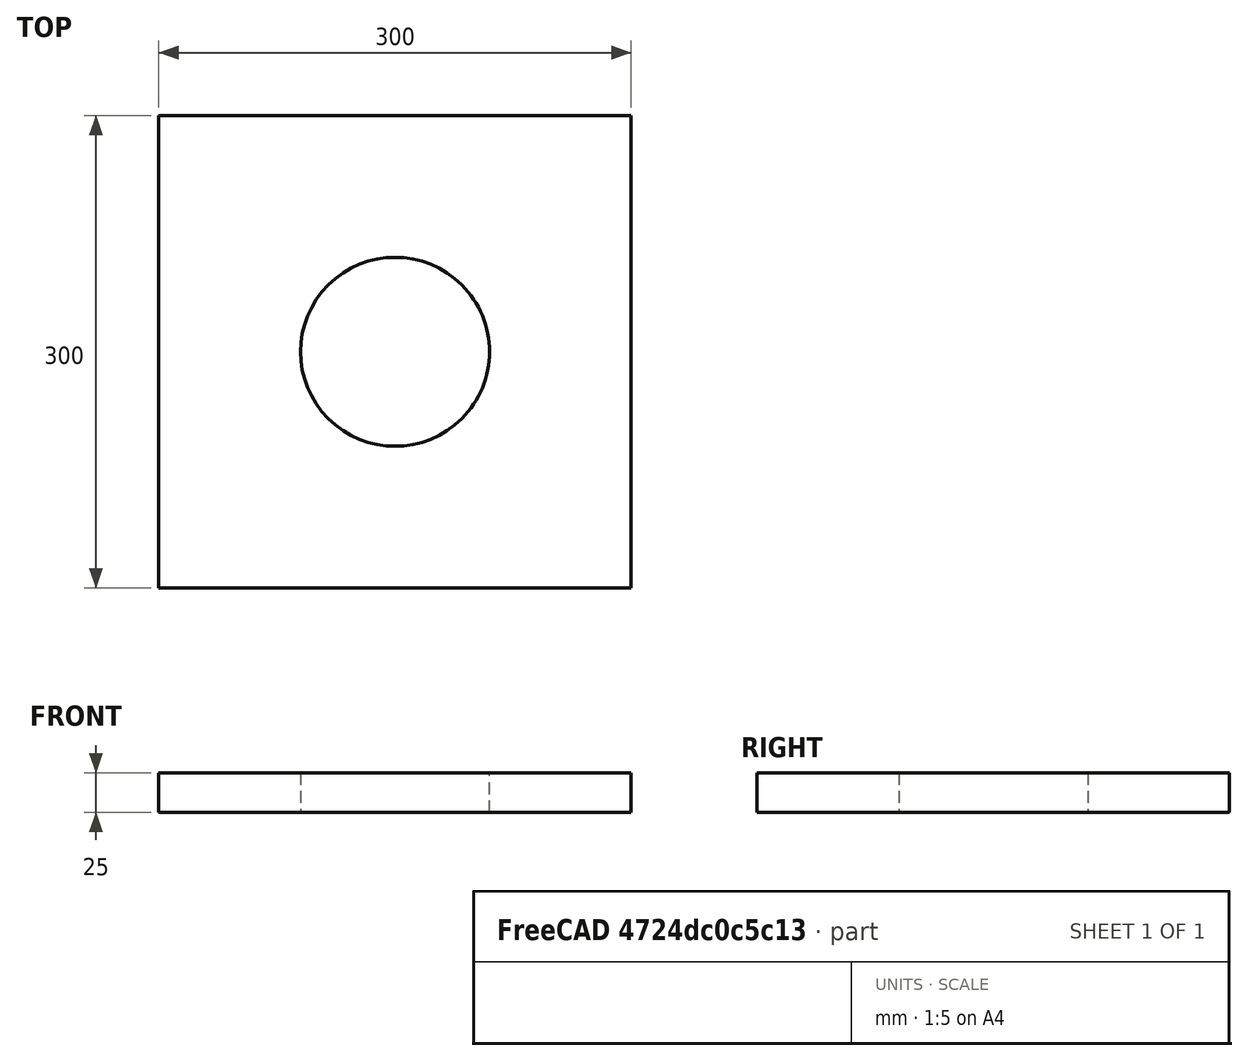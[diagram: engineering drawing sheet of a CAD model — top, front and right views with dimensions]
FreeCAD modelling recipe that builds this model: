
FCSTD DOCUMENT  (FreeCAD 0.21R33694 (Git))
Label: Lug_Displacement_Example
License: All rights reserved
LicenseURL: http://en.wikipedia.org/wiki/All_rights_reserved
objects: Part::FeaturePython×5, Sketcher::SketchObject×2, Part::Extrusion×2, Fem::FemMeshObjectPython×2, Fem::FemSolverObjectPython×1, Fem::ConstraintFixed×1, Fem::ConstraintPressure×1, Part::MultiFuse×1, App::MaterialObjectPython×1, Fem::ConstraintDisplacement×1, Fem::FemResultObjectPython×1, Fem::FemAnalysis×1
note: 10 computed .brp shape members not serialized (recipe doc carries the construction recipe); baked Part::Feature solids carry a one-line shape summary decoded from their .brp

FEATURE [Sketcher::SketchObject] Sketch
  FullyConstrained = true
  Placement = pos=(150,0,0) rot=(0,0,1;0rad)
  sketch-geometry (5):
    g0: LineSegment StartX=0 StartY=0 StartZ=0 EndX=300 EndY=0 EndZ=0
    g1: LineSegment StartX=300 StartY=0 StartZ=0 EndX=300 EndY=300 EndZ=0
    g2: LineSegment StartX=300 StartY=300 StartZ=0 EndX=0 EndY=300 EndZ=0
    g3: LineSegment StartX=0 StartY=300 StartZ=0 EndX=0 EndY=0 EndZ=0
    g4: Circle CenterX=150 CenterY=150 CenterZ=0 NormalX=0 NormalY=0 NormalZ=1 AngleXU=0 Radius=60
  constraints (14):
    c: Coincident(g0,g1)
    c: Coincident(g1,g2)
    c: Coincident(g2,g3)
    c: Coincident(g3,g0)
    c: Horizontal(g0)
    c: Horizontal(g2)
    c: Vertical(g1)
    c: Vertical(g3)
    c: Coincident(g0,g-1)
    c: DistanceY(g1,g1) = 300
    c: DistanceX(g0,g0) = 300
    c: DistanceX(g0,g4) = 150
    c: DistanceY(g0,g4) = 150
    c: Radius(g4) = 60
FEATURE [Part::Extrusion] Extrude
  Base = -> Sketch
  Dir = (0,0,1)
  DirMode = 2
  FaceMakerClass = Part::FaceMakerBullseye
  LengthFwd = 25
  LengthRev = 0
  Solid = true
  Symmetric = false
FEATURE [Fem::FemSolverObjectPython] SolverCcxTools  # FEM object (typed FeaturePython)
  AnalysisType = 0
  BeamShellResultOutput3D = false
  BucklingFactors = 1
  EigenmodeHighLimit = 1000000
  EigenmodeLowLimit = 0
  EigenmodesCount = 10
  GeometricalNonlinearity = 0
  IterationsControlParameterCutb = 0.25,0.5,0.75,0.85,,,1.5,
  IterationsControlParameterIter = 4,8,9,200,10,400,,200,,
  IterationsControlParameterTimeUse = false
  IterationsThermoMechMaximum = 200
  IterationsUserDefinedIncrementations = false
  IterationsUserDefinedTimeStepLength = false
  MaterialNonlinearity = 0
  MatrixSolverType = 0
  SplitInputWriter = false
  ThermoMechSteadyState = true
  TimeEnd = 1
  TimeInitialStep = 1
FEATURE [Fem::ConstraintFixed] ConstraintFixed001
  NormalDirection = (0,-1,0)
  Normals = (16) [(0,-1,0),(0,-1,0),(0,-1,0),(0,-1,0),(0,-1,0),(0,-1,0),(0,-1,0),(0,-1,0),(0,-1,0),(0,-1,0),(0,-1,0),(0,-1,0),(0,-1,0),(0,-1,0),(0,-1,0),(0,-1,0)]
  Points = (16) [(150,0,25),(250,0,25),(350,0,25),(450,0,25),(150,0,16.6667),(250,0,16.6667),(350,0,16.6667),(450,0,16.6667),(150,0,8.33333),(250,0,8.33333),+6 more]
  References = -> [Extrude]
  Scale = 13
FEATURE [Fem::ConstraintPressure] ConstraintPressure
  NormalDirection = (1,-1e-16,0)
  Normals = (16) [(-1,0,0),(0.5,-0.866025,0),(0.5,0.866025,0),(-1,2.44929e-16,0),(-1,0,0),(0.5,-0.866025,0),(0.5,0.866025,0),(-1,2.44929e-16,0),(-1,0,0),+7 more]
  Points = (16) [(360,150,25),(270,201.962,25),(270,98.0385,25),(360,150,25),(360,150,16.6667),(270,201.962,16.6667),(270,98.0385,16.6667),(360,150,16.6667),+8 more]
  Pressure = 100
  References = -> [Extrude]
  Scale = 15
FEATURE [Sketcher::SketchObject] Sketch001
  FullyConstrained = true
  sketch-geometry (2):
    g0: LineSegment StartX=150 StartY=300 StartZ=0 EndX=450 EndY=0 EndZ=0
    g1: LineSegment StartX=150 StartY=0 StartZ=0 EndX=450 EndY=300 EndZ=0
  constraints (8):
    c: DistanceX(g1) = 150
    c: DistanceY(g1,g-1) = 0
    c: DistanceY(g0,g-1) = 0
    c: DistanceX(g1,g0) = 300
    c: DistanceX(g-1,g0) = 150
    c: DistanceX(g-1,g1) = 450
    c: DistanceY(g-1,g0) = 300
    c: DistanceY(g-1,g1) = 300
FEATURE [Part::Extrusion] Extrude001
  Base = -> Sketch001
  Dir = (0,0,1)
  DirMode = 0
  FaceMakerClass = Part::FaceMakerBullseye
  LengthFwd = 25
  LengthRev = 0
  Solid = false
  Symmetric = false
FEATURE [Part::FeaturePython] Slice  # WARN: FeaturePython — macro-defined, semantics opaque (R4)
  Base = -> Extrude
  Mode = 1
  Tolerance = 0
  Tools = -> [Extrude001]
FEATURE [Part::FeaturePython] Slice_child0  label="Slice.0"  # WARN: FeaturePython — macro-defined, semantics opaque (R4)
  Base = -> Slice
  FilterType = 1
  Invert = false
  OverrideMaxVal = 0
  WindowFrom = 80
  WindowTo = 100
  items = 0
FEATURE [Part::FeaturePython] Slice_child1  label="Slice.1"  # WARN: FeaturePython — macro-defined, semantics opaque (R4)
  Base = -> Slice
  FilterType = 1
  Invert = false
  OverrideMaxVal = 0
  WindowFrom = 80
  WindowTo = 100
  items = 1
FEATURE [Part::FeaturePython] Slice_child2  label="Slice.2"  # WARN: FeaturePython — macro-defined, semantics opaque (R4)
  Base = -> Slice
  FilterType = 1
  Invert = false
  OverrideMaxVal = 0
  WindowFrom = 80
  WindowTo = 100
  items = 2
FEATURE [Part::FeaturePython] Slice_child3  label="Slice.3"  # WARN: FeaturePython — macro-defined, semantics opaque (R4)
  Base = -> Slice
  FilterType = 1
  Invert = false
  OverrideMaxVal = 0
  WindowFrom = 80
  WindowTo = 100
  items = 3
FEATURE [Part::MultiFuse] Fusion001  label="Fusion_25mm"
  Shapes = -> [Slice_child0,Slice_child1,Slice_child2,Slice_child3]
FEATURE [App::MaterialObjectPython] MaterialSolid  # material (typed FeaturePython)
  Category = 0
  Material = AuthorAndLicense=(c) 2014 M. Münch - GNU Lesser General Public License (LGPL),CardName=Steel-St-E-315,Density=7800 kg/m^3,Father=Metal,+13 more (map truncated)
FEATURE [Fem::FemMeshObjectPython] FEMMeshGmsh  # FEM object (typed FeaturePython)
  Algorithm2D = 0
  Algorithm3D = 0
  CharacteristicLengthMax = 0
  CharacteristicLengthMin = 0
  CoherenceMesh = true
  ElementDimension = 0
  ElementOrder = 1
  GeometryTolerance = 1e-06
  GroupsOfNodes = false
  HighOrderOptimize = 0
  MeshSizeFromCurvature = 12
  OptimizeNetgen = false
  OptimizeStd = true
  Part = -> Fusion001
  RecombinationAlgorithm = 0
  Recombine3DAll = false
  RecombineAll = false
  SecondOrderLinear = false
FEATURE [Fem::ConstraintDisplacement] ConstraintDisplacement
  NormalDirection = (1.04e-14,-1,0)
  Normals = (16) [(-0.707107,-0.707107,0),(-0.258819,-0.965926,0),(0.258819,-0.965926,0),(0.707107,-0.707107,0),(-0.707107,-0.707107,0),(-0.258819,-0.965926,0),+10 more]
  Points = (16) [(342.426,192.426,25),(315.529,207.956,25),(284.471,207.956,25),(257.574,192.426,25),(342.426,192.426,16.6667),(315.529,207.956,16.6667),+10 more]
  References = -> [Fusion001]
  Scale = 7
  hasXFormula = false
  hasYFormula = false
  hasZFormula = false
  rotxFix = false
  rotxFree = true
  rotyFix = false
  rotyFree = true
  rotzFix = false
  rotzFree = true
  useFlowSurfaceForce = false
  xDisplacement = 0
  xFix = false
  xFree = true
  xRotation = 0
  yDisplacement = 1
  yFix = false
  yFree = false
  yRotation = 0
  zDisplacement = 0
  zFix = false
  zFree = true
  zRotation = 0
FEATURE [Fem::FemMeshObjectPython] Result_Mesh_Volume  # FEM object (typed FeaturePython)
FEATURE [Fem::FemResultObjectPython] ResultMechanical  # FEM object (typed FeaturePython)
  CriticalStrainRatio = [0,0,0,0,0,0,0,0,0.000396986,0.000447757,0.000434295,0.00106615,0.0581688,0.115378,0.0244695,0.0776566,0.0192562,0.0787961,0,0,0,0,0,0,0,0,0,0,0,0,0,0,0,0,0,0,0,0,0,0,0,0,0,0,0,0,0,0,0,0,0,0,0,-0.00253402,0,0,0,0,0,0,0,0,0,0,0,0,0,0,+1416 more]
  DisplacementLengths = [0,0,0,0,0.00658583,0.00654723,0.00719904,0.00728292,0.00181296,0.00144701,0.00147876,0.00188107,0.0180657,0.0179329,0.0057014,0.0180954,0.00589517,0.0183705,0,0,0,0,0,0,0,0,0,0,0,0,0,0,0,0,0,0,0,0,0,0,0,0,0,0,0,0,0,0,0,0,0.00656804,+1433 more]
  DisplacementVectors = (1484) [(0,0,0),(0,0,0),(0,0,0),(0,0,0),(-0.00658228,0.000212972,-3.77015e-05),(-0.00653963,0.000313392,-3.40754e-05),(0.00710179,0.000383461,-0.00111527),+1477 more]
  Eigenmode = 0
  EigenmodeFrequency = 0
  Mesh = -> Result_Mesh_Volume
  NodeNumbers = [1,2,3,4,5,6,7,8,9,10,11,12,13,14,15,16,17,18,19,20,21,22,23,24,25,26,27,28,29,30,31,32,33,34,35,36,37,38,39,40,41,42,43,44,45,46,47,48,49,50,51,52,53,54,55,56,57,58,59,60,61,62,63,64,65,66,67,68,69,+1415 more]
  NodeStressXX = [13.426,16.4199,13.4556,16.0408,-2.09905,-1.38256,-2.01983,-2.28136,-39.5186,-22.746,-23.3476,-41.1073,-48.7291,-65.9297,-178.587,-35.0021,-201.476,-67.5779,11.5836,11.2584,23.5952,14.5874,-0.536989,-6.67125,-0.222188,14.3087,26.847,30.5357,+1456 more]
  NodeStressXY = [-3.72009,-3.0923,3.5271,3.17441,-0.350484,0.039559,0.490638,0.534001,-150.675,152.266,-155.977,144.706,130.07,137.412,-21.7469,-127.585,5.75774,-130.649,-4.71168,4.69743,-31.0898,-40.9487,-28.1196,0.145656,27.3688,39.5976,31.1546,-19.9127,+1456 more]
  NodeStressXZ = [3.50697,-3.75392,-3.38473,3.78417,-0.36904,0.585293,0.387141,-0.430337,-1.3387,-0.573118,0.0621941,0.864059,-0.102491,4.18446,6.67088,7.91318,-5.0812,-2.67053,-8.01099e-15,1.73492e-14,-0.12283,-0.431082,0.495674,-0.00238664,-0.443662,+1459 more]
  NodeStressYY = [39.9407,48.5871,39.1819,47.7946,-2.92011,-3.29463,-2.98892,-2.9634,-31.1879,-41.4036,-37.4424,-47.1158,-97.3686,-126.379,102.369,-91.6432,82.6509,-75.6608,27.0284,26.2696,65.195,34.0222,-5.29159,-20.1338,-3.61904,34.7322,66.5174,71.2499,+1456 more]
  NodeStressYZ = [4.12725,-3.62927,3.32768,-4.30827,0.522758,-0.118543,0.369485,-0.27184,-4.27725,-1.51038,2.37579,4.21234,8.70691,-4.22039,5.33743,6.70062,-2.12425,6.39698,0.503378,-0.287412,7.69914,6.81822,0.722123,-0.431255,0.986269,4.20535,10.9657,+1457 more]
  NodeStressZZ = [13.3854,15.638,13.2459,15.3076,-0.253691,-0.136898,-0.28411,-0.354085,-5.69476,-3.60816,-2.16034,-5.57463,6.14457,-20.095,3.58656,9.82804,-6.05515,-0.0472891,11.5836,11.2584,21.4353,14.5829,-2.64425,-5.81508,-1.7916,9.71454,28.0093,30.5357,+1456 more]
  Peeq = [0,0,0,0,0,0,0,0,0.000200824,0.000223595,0.000216449,0.000540151,0.0413252,0.0473404,0.0113741,0.0419901,0.0114293,0.0479716,0,0,0,0,0,0,0,0,0,0,0,0,0,0,0,0,0,0,0,0,0,0,0,0,0,0,0,0,0,0,0,0,0,0,0,-0.000605359,0,0,0,0,0,0,0,0,0,0,0,0,0,0,+1416 more]
  ResultType = Fem::ResultMechanical
  Stats = [0,0,0,0,0,0,0,0,0,0,0,0,0,0,0,0,0,0,0,0,0,0,0,0,0,0]
  Time = 0
FEATURE [Fem::FemAnalysis] Analysis
  Group = -> [SolverCcxTools,MaterialSolid,ConstraintFixed001,ConstraintPressure,FEMMeshGmsh,ConstraintDisplacement,ResultMechanical]
